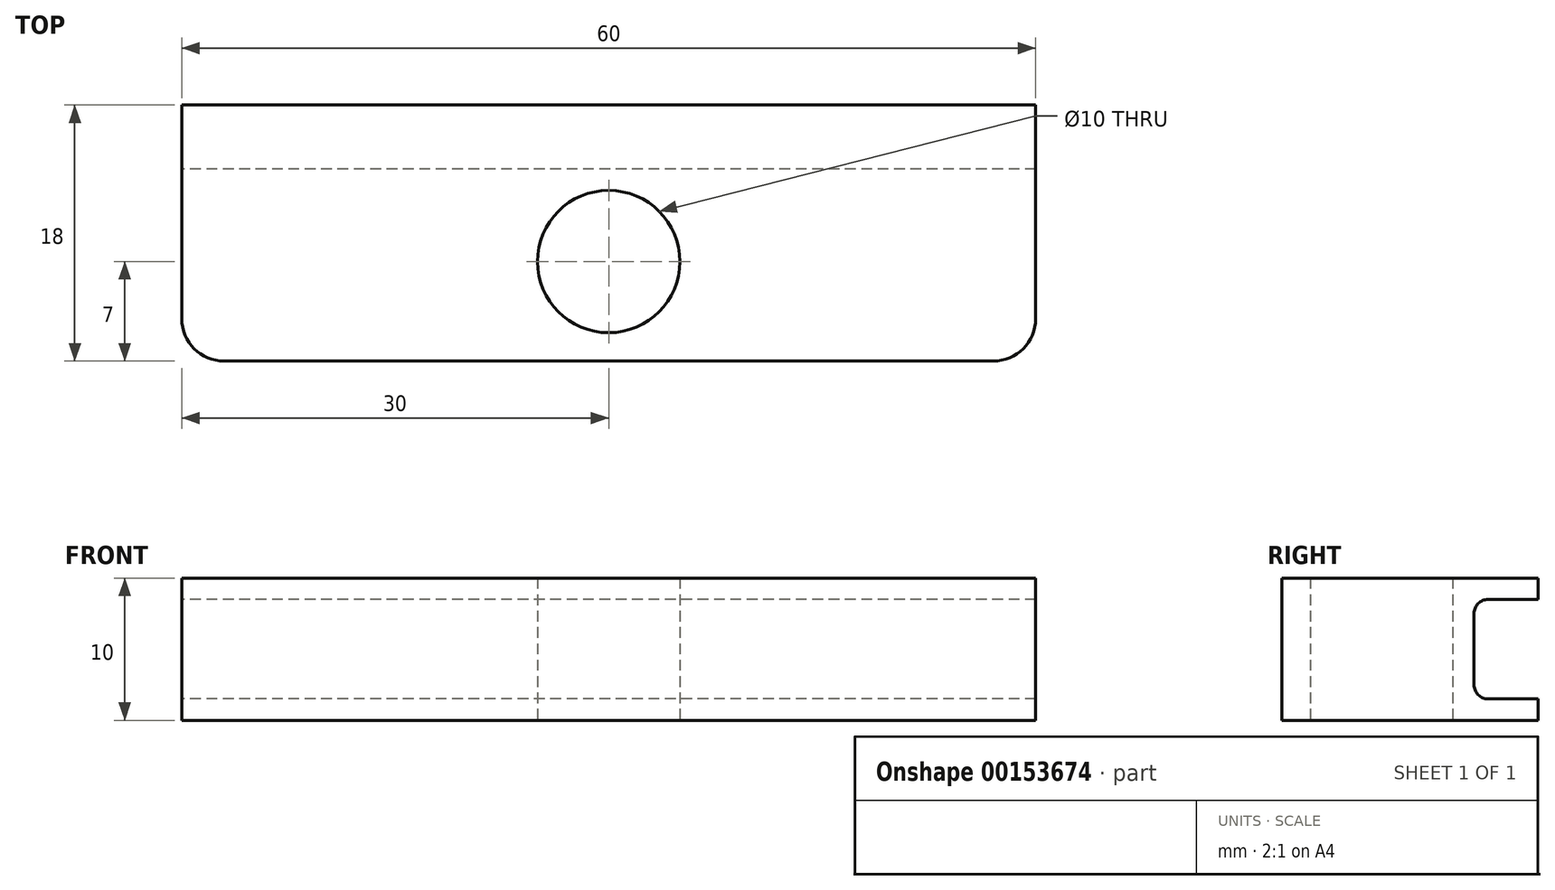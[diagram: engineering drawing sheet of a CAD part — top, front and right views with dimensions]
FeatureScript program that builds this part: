
annotation { "Feature Type Name" : "Feature", "Feature Type Description" : "" }
export const myFeature = defineFeature(function(context is Context, id is Id, definition is map)
    precondition{}
    {
        {
            var Q0;
            Q0=qCreatedBy(makeId("Top.planeOp"),FACE);
            var sketch = newSketch(context, id + "F0", { "sketchPlane" : qUnion([Q0])});
            skLineSegment(sketch, "E0.bottom", {"start": v(-30, 0) * mm, "end": v(30, 0) * mm});
            skLineSegment(sketch, "E0.top", {"start": v(-30, -18) * mm, "end": v(30, -18) * mm});
            skLineSegment(sketch, "E0.left", {"start": v(-30, 0) * mm, "end": v(-30, -18) * mm});
            skLineSegment(sketch, "E0.right", {"start": v(30, 0) * mm, "end": v(30, -18) * mm});
            skCircle(sketch, "E1", {"center": v(0, -11) * mm, "radius": 5 * mm});
            skSolve(sketch);
        }
        {
            var Q0;
            Q0=makeQuery(id+"F0.imprint","IMPRINT",FACE,{"disambiguationData":[TD([[makeQuery(id+"F0.imprint","IMPRINT",EDGE,{"derivedFrom":sQuery(id+"F0.wireOp",EDGE,"E0.bottom")}),-1.0]])]});
            extrude(context, id + "F1", {"entities" : qUnion([Q0]), "depth" : 10 * mm});
        }
        {
            var Q0;
            Q0=makeQuery(id+"F1.opExtrude","SWEPT_EDGE",EDGE,{"disambiguationData":[OSD([sQuery(id+"F0.wireOp",EDGE,"E0.top"),sQuery(id+"F0.wireOp",EDGE,"E0.left")])]});
            var Q1;
            Q1=makeQuery(id+"F1.opExtrude","SWEPT_EDGE",EDGE,{"disambiguationData":[OSD([sQuery(id+"F0.wireOp",EDGE,"E0.top"),sQuery(id+"F0.wireOp",EDGE,"E0.right")])]});
            fillet(context, id + "F2", {"entities" : qUnion([Q0, Q1]), "radius" : 3 * mm, "tangentPropagation" : true, "allowEdgeOverflow" : false});
        }
        {
            var Q0;
            Q0=makeQuery(id+"F1.opExtrude","SWEPT_FACE",FACE,{"disambiguationData":[OSD([sQuery(id+"F0.wireOp",EDGE,"E0.bottom")])]});
            var sketch = newSketch(context, id + "F3", { "sketchPlane" : qUnion([Q0])});
            skLineSegment(sketch, "E2.bottom", {"start": v(-30, 8.5) * mm, "end": v(30, 8.5) * mm});
            skLineSegment(sketch, "E2.top", {"start": v(-30, 1.5) * mm, "end": v(30, 1.5) * mm});
            skLineSegment(sketch, "E2.left", {"start": v(-30, 8.5) * mm, "end": v(-30, 1.5) * mm});
            skLineSegment(sketch, "E2.right", {"start": v(30, 8.5) * mm, "end": v(30, 1.5) * mm});
            skSolve(sketch);
        }
        {
            var Q0;
            Q0 = qSketchRegion(id + "F3", true);
            var Q1;
            Q1=makeQuery(id+"F3.imprint","IMPRINT",FACE,{"disambiguationData":[TD([[makeQuery(id+"F3.imprint","IMPRINT",EDGE,{"derivedFrom":sQuery(id+"F3.wireOp",EDGE,"E2.bottom")}),-1.0]])]});
            extrude(context, id + "F4", {"entities" : qUnion([Q0, Q1]), "operationType" : NewBodyOperationType.REMOVE, "oppositeDirection" : true, "depth" : 4.5 * mm});
        }
        {
            var Q0;
            Q0=makeQuery(id+"F4.boolean.opBoolean","COPY",EDGE,{"derivedFrom":makeQuery(id+"F4.opExtrude","CAP_EDGE",EDGE,{"disambiguationData":[OSD([sQuery(id+"F3.wireOp",EDGE,"E2.bottom")])],"isStart":false})});
            var Q1;
            Q1=makeQuery(id+"F4.boolean.opBoolean","COPY",EDGE,{"derivedFrom":makeQuery(id+"F4.opExtrude","CAP_EDGE",EDGE,{"disambiguationData":[OSD([sQuery(id+"F3.wireOp",EDGE,"E2.top")])],"isStart":false})});
            fillet(context, id + "F5", {"entities" : qUnion([Q0, Q1]), "radius" : 1 * mm, "tangentPropagation" : true, "allowEdgeOverflow" : false});
        }
    });
